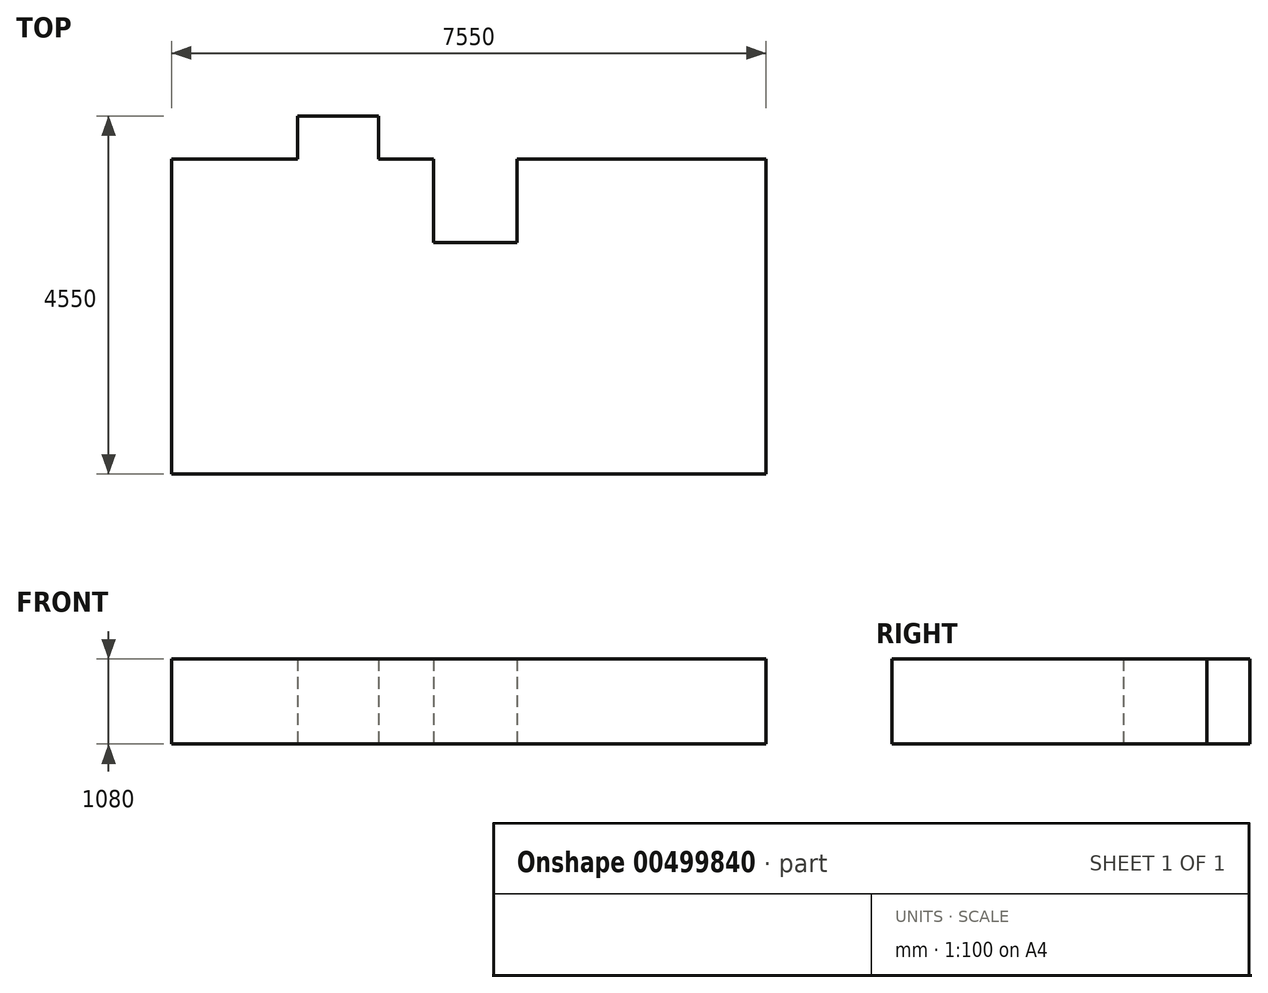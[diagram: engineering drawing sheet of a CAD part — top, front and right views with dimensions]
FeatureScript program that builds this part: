
annotation { "Feature Type Name" : "Feature", "Feature Type Description" : "" }
export const myFeature = defineFeature(function(context is Context, id is Id, definition is map)
    precondition{}
    {
        {
            var Q0;
            Q0=qCreatedBy(makeId("Top.planeOp"),FACE);
            var sketch = newSketch(context, id + "F0", { "sketchPlane" : qUnion([Q0])});
            skLineSegment(sketch, "E0", {"start": v(-9750, 0) * mm, "end": v(-1810, 0) * mm});
            skLineSegment(sketch, "E1", {"start": v(-9750, 0) * mm, "end": v(-9750, -2400) * mm});
            skLineSegment(sketch, "E2", {"start": v(-9750, -2400) * mm, "end": v(-9750, -2950) * mm});
            skLineSegment(sketch, "E3", {"start": v(-9750, -2950) * mm, "end": v(-9750, -6950) * mm});
            skLineSegment(sketch, "E4", {"start": v(-9750, -6950) * mm, "end": v(-2200, -6950) * mm});
            skLineSegment(sketch, "E5", {"start": v(-2200, -6950) * mm, "end": v(-2200, -2950) * mm});
            skLineSegment(sketch, "E6", {"start": v(-2200, -2950) * mm, "end": v(-7120, -2950) * mm});
            skLineSegment(sketch, "E7", {"start": v(-7120, -2950) * mm, "end": v(-7120, -2400) * mm});
            skLineSegment(sketch, "E8", {"start": v(-7120, -2400) * mm, "end": v(-6900, -2400) * mm});
            skLineSegment(sketch, "E9", {"start": v(-6900, -2400) * mm, "end": v(-6900, -2680) * mm});
            skLineSegment(sketch, "E10", {"start": v(-6900, -2680) * mm, "end": v(-1815, -2680) * mm});
            skLineSegment(sketch, "E11", {"start": v(-1815, -2680) * mm, "end": v(-1815, -2330) * mm});
            skLineSegment(sketch, "E12", {"start": v(-1815, -2330) * mm, "end": v(0, -2330) * mm});
            skLineSegment(sketch, "E13", {"start": v(0, -2330) * mm, "end": v(0, -1090) * mm});
            skLineSegment(sketch, "E14", {"start": v(0, -1090) * mm, "end": v(0, -240) * mm});
            skLineSegment(sketch, "E15", {"start": v(0, -240) * mm, "end": v(0, 0) * mm});
            skLineSegment(sketch, "E16", {"start": v(0, 0) * mm, "end": v(-9750, 0) * mm});
            skLineSegment(sketch, "E17", {"start": v(-9750, -2400) * mm, "end": v(-8150, -2400) * mm});
            skLineSegment(sketch, "E18", {"start": v(-8150, -2400) * mm, "end": v(-8150, -2950) * mm});
            skLineSegment(sketch, "E19", {"start": v(-8150, -2950) * mm, "end": v(-9750, -2950) * mm});
            skLineSegment(sketch, "E20", {"start": v(-6420, -2950) * mm, "end": v(-6420, -4010) * mm});
            skLineSegment(sketch, "E21", {"start": v(-6420, -4010) * mm, "end": v(-5360, -4010) * mm});
            skLineSegment(sketch, "E22", {"start": v(-5360, -4010) * mm, "end": v(-5360, -2950) * mm});
            skLineSegment(sketch, "E23", {"start": v(0, 0) * mm, "end": v(145, 0) * mm});
            skLineSegment(sketch, "E24", {"start": v(145, 0) * mm, "end": v(145, -5370) * mm});
            skLineSegment(sketch, "E25", {"start": v(145, -5370) * mm, "end": v(0, -5370) * mm});
            skLineSegment(sketch, "E26", {"start": v(0, -5370) * mm, "end": v(0, -2330) * mm});
            skLineSegment(sketch, "E27", {"start": v(0, -2475) * mm, "end": v(-1670, -2475) * mm});
            skLineSegment(sketch, "E28", {"start": v(-1670, -2475) * mm, "end": v(-1670, -2950) * mm});
            skLineSegment(sketch, "E29", {"start": v(-1670, -2950) * mm, "end": v(-1900, -2950) * mm});
            skLineSegment(sketch, "E30", {"start": v(-1900, -2950) * mm, "end": v(-1900, -7250) * mm});
            skLineSegment(sketch, "E31", {"start": v(-1900, -7250) * mm, "end": v(-2200, -6950) * mm});
            skLineSegment(sketch, "E32", {"start": v(-1900, -7250) * mm, "end": v(-10050, -7250) * mm});
            skLineSegment(sketch, "E33", {"start": v(-10050, -7250) * mm, "end": v(-9750, -6950) * mm});
            skLineSegment(sketch, "E34", {"start": v(-10050, -7250) * mm, "end": v(-10050, 300) * mm});
            skLineSegment(sketch, "E35", {"start": v(-10050, 300) * mm, "end": v(-9750, 0) * mm});
            skLineSegment(sketch, "E36", {"start": v(-10050, 300) * mm, "end": v(145, 300) * mm});
            skLineSegment(sketch, "E37", {"start": v(145, 300) * mm, "end": v(145, 0) * mm});
            skLineSegment(sketch, "E38", {"start": v(-8150, -2400) * mm, "end": v(-7120, -2400) * mm});
            skSolve(sketch);
        }
        {
            var Q0;
            Q0=qCreatedBy(makeId("Front.planeOp"),FACE);
            var sketch = newSketch(context, id + "F1", { "sketchPlane" : qUnion([Q0])});
            skLineSegment(sketch, "E39", {"start": v(-1810, 0) * mm, "end": v(-1810, 210) * mm});
            skLineSegment(sketch, "E40", {"start": v(-1810, 210) * mm, "end": v(-2080, 210) * mm});
            skLineSegment(sketch, "E41", {"start": v(-2080, 210) * mm, "end": v(-2080, 380) * mm});
            skLineSegment(sketch, "E42", {"start": v(-2080, 380) * mm, "end": v(-7320, 380) * mm});
            skLineSegment(sketch, "E43", {"start": v(-7320, 380) * mm, "end": v(-7320, 1080) * mm});
            skLineSegment(sketch, "E44", {"start": v(-7320, 1080) * mm, "end": v(-9750, 1080) * mm});
            skLineSegment(sketch, "E45", {"start": v(-9750, 1080) * mm, "end": v(-9750, 0) * mm});
            skLineSegment(sketch, "E46", {"start": v(-9750, 0) * mm, "end": v(-1810, 0) * mm});
            skSolve(sketch);
        }
        {
            var Q0;
            Q0=makeQuery(id+"F0.imprint","IMPRINT",FACE,{"disambiguationData":[TD([[makeQuery(id+"F0.imprint","IMPRINT",EDGE,{"derivedFrom":sQuery(id+"F0.wireOp",EDGE,"E3")}),1.0]])]});
            var Q1;
            Q1=sQuery(id+"F1.wireOp",VERTEX,"E45.start");
            extrude(context, id + "F2", {"entities" : qUnion([Q0]), "endBound" : BoundingType.UP_TO_VERTEX, "endBoundEntityVertex" : qUnion([Q1]), "depth" : 25 * mm});
        }
    });
